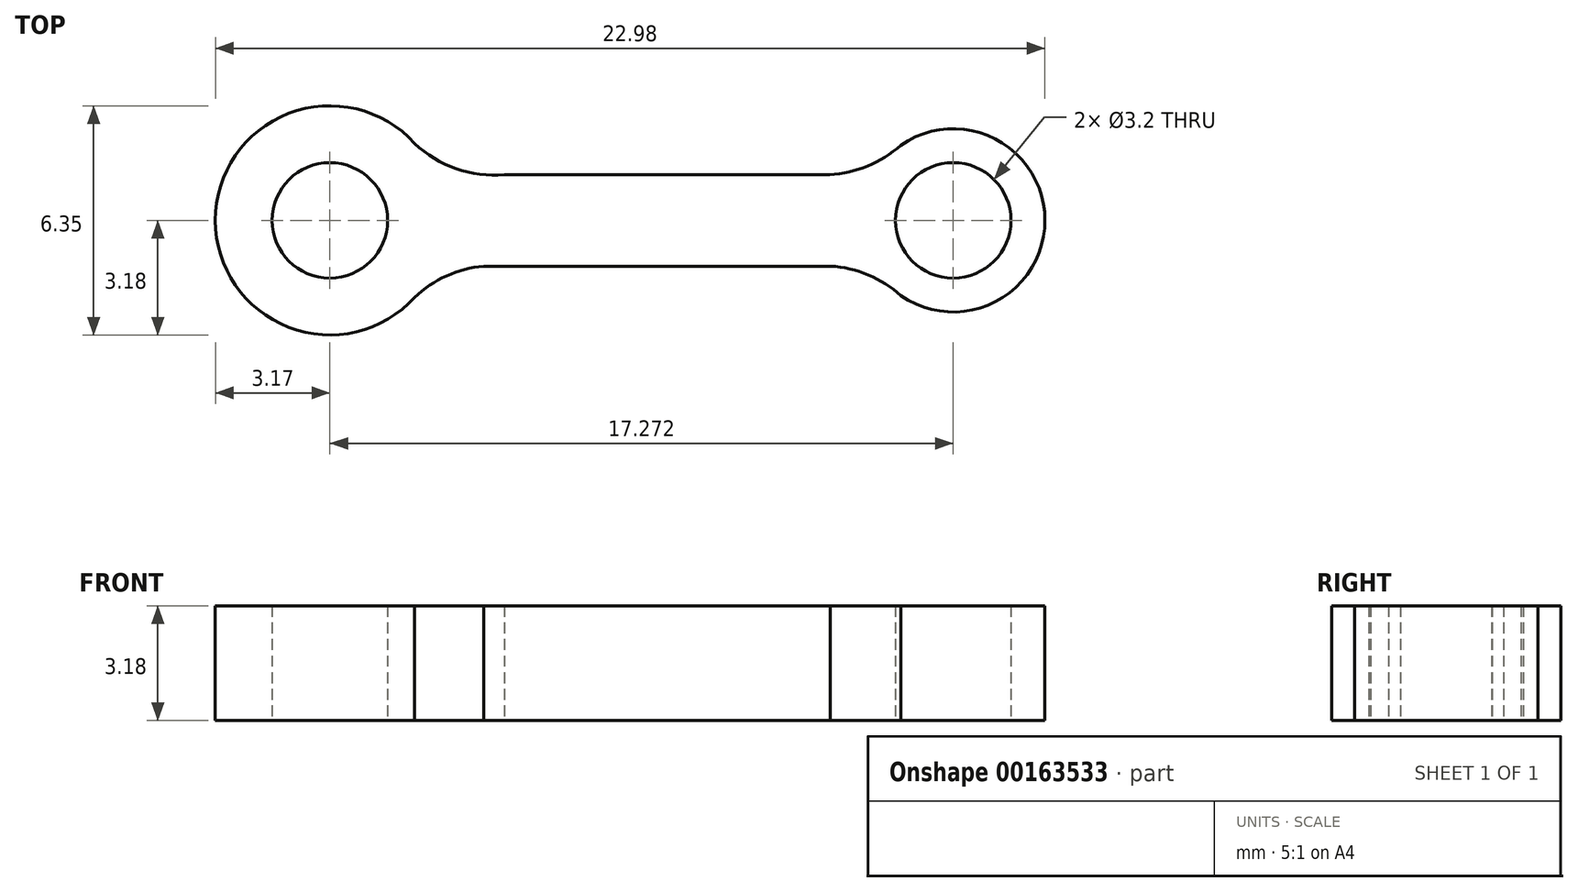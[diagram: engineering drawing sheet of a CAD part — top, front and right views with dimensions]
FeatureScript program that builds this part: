
annotation { "Feature Type Name" : "Feature", "Feature Type Description" : "" }
export const myFeature = defineFeature(function(context is Context, id is Id, definition is map)
    precondition{}
    {
        {
            var Q0;
            Q0=qCreatedBy(makeId("Top.planeOp"),FACE);
            var sketch = newSketch(context, id + "F0", { "sketchPlane" : qUnion([Q0])});
            skCircle(sketch, "E0", {"center": v(0, 0) * mm, "radius": 1.6 * mm});
            skArc(sketch, "E1", {"start": v(2.35, 2.13) * mm, "mid": v(-3.18, 0) * mm, "end": v(2.35, -2.13) * mm});
            skCircle(sketch, "E2", {"center": v(17.27, 0) * mm, "radius": 1.6 * mm});
            skArc(sketch, "E3", {"start": v(15.82, -2.09) * mm, "mid": v(19.81, 0) * mm, "end": v(15.82, 2.08) * mm});
            skLineSegment(sketch, "E4", {"start": v(0, 0) * mm, "end": v(17.27, 0) * mm, "construction": true});
            skLineSegment(sketch, "E5", {"start": v(4.26, -1.27) * mm, "end": v(13.87, -1.27) * mm});
            skLineSegment(sketch, "E6", {"start": v(13.7, 6.33) * mm, "end": v(13.7, -4.87) * mm, "construction": true});
            skLineSegment(sketch, "E7", {"start": v(4.55, 4.68) * mm, "end": v(4.55, -6.94) * mm, "construction": true});
            skLineSegment(sketch, "E8", {"start": v(-1.5, 4.45) * mm, "end": v(17.1, 4.45) * mm, "construction": true});
            skLineSegment(sketch, "E9", {"start": v(1.44, -4.45) * mm, "end": v(14, -4.45) * mm, "construction": true});
            skArc(sketch, "E10", {"start": v(2.35, 2.13) * mm, "mid": v(3.5, 1.43) * mm, "end": v(4.83, 1.27) * mm});
            skArc(sketch, "E11", {"start": v(4.26, -1.27) * mm, "mid": v(3.23, -1.54) * mm, "end": v(2.35, -2.13) * mm});
            skArc(sketch, "E12", {"start": v(15.82, -2.09) * mm, "mid": v(14.92, -1.51) * mm, "end": v(13.87, -1.27) * mm});
            skLineSegment(sketch, "E13.trimOffspring", {"start": v(4.83, 1.27) * mm, "end": v(13.84, 1.27) * mm});
            skArc(sketch, "E14.trimOffspring", {"start": v(13.84, 1.27) * mm, "mid": v(14.9, 1.5) * mm, "end": v(15.82, 2.08) * mm});
            skSolve(sketch);
        }
        {
            var Q0;
            Q0 = qSketchRegion(id + "F0", true);
            extrude(context, id + "F1", {"entities" : qUnion([Q0]), "depth" : 3.17 * mm});
        }
    });
